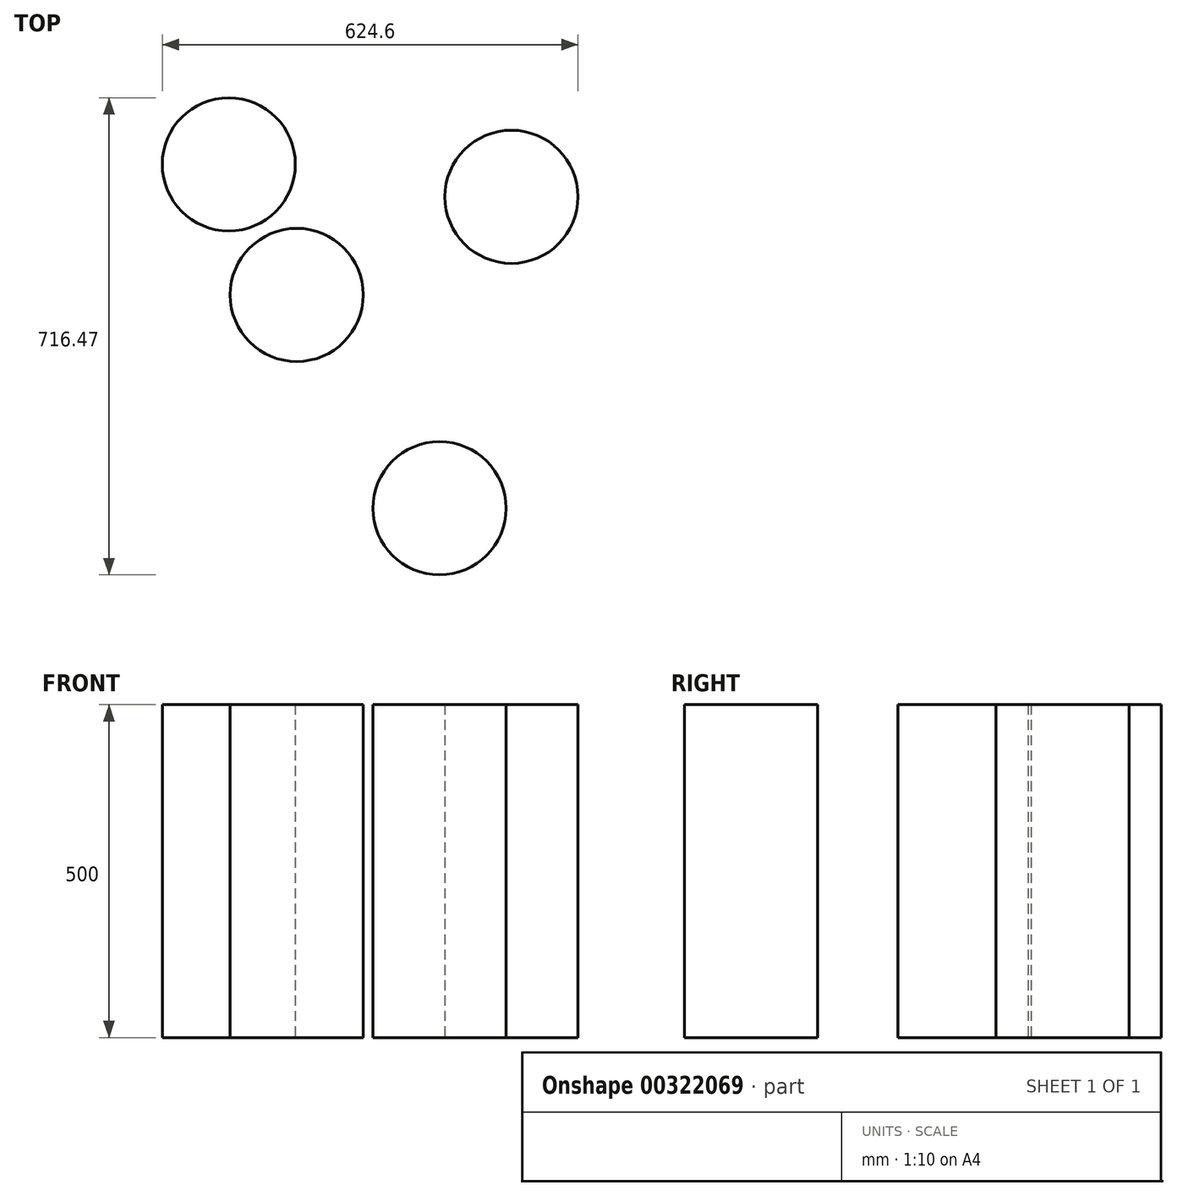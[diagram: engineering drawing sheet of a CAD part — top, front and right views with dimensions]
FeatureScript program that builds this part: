
annotation { "Feature Type Name" : "Feature", "Feature Type Description" : "" }
export const myFeature = defineFeature(function(context is Context, id is Id, definition is map)
    precondition{}
    {
        {
            var Q0;
            Q0=qCreatedBy(makeId("Top.planeOp"),FACE);
            var sketch = newSketch(context, id + "F0", { "sketchPlane" : qUnion([Q0])});
            skCircle(sketch, "E0", {"center": v(-266.33, 228.95) * mm, "radius": 100 * mm});
            skCircle(sketch, "E1", {"center": v(-164.3, 32.83) * mm, "radius": 100 * mm});
            skCircle(sketch, "E2", {"center": v(50.23, -287.52) * mm, "radius": 100 * mm});
            skCircle(sketch, "E3", {"center": v(158.27, 180.23) * mm, "radius": 100 * mm});
            skSolve(sketch);
        }
        {
            var Q0;
            Q0=qSketchRegion(id+"F0",true);
            extrude(context, id + "F1", {"entities" : qUnion([Q0]), "depth" : 500 * mm});
        }
    });
